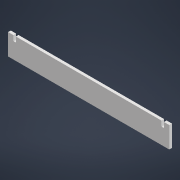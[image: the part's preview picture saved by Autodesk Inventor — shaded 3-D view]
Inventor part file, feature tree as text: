
AUTODESK INVENTOR PART (.ipt)
format: ipt  version: 2021.3 (Build 253353000, 353)  size: 116,224 bytes
history: native  units: in
note: dims shown in document units (in); Inventor stores cm internally (conversion verified against a paired STEP export)
features: extrude x1, sketch x1
ambient origin geometry x8: Origin, YZ Plane, XZ Plane, XY Plane, X Axis, Y Axis, Z Axis, Center Point
bodies: Solid1 (feature_tree)
feature tree (2):
  extrude  "Extrusion1"  Depth=2.0in
  sketch  "Sketch1"  dims[d0=15.2413in d1=2.0in d2=0.5in d3=0.5in d4=0.23in d5=0.5in d6=0.25in d7=0.0in d8=0.05in]
